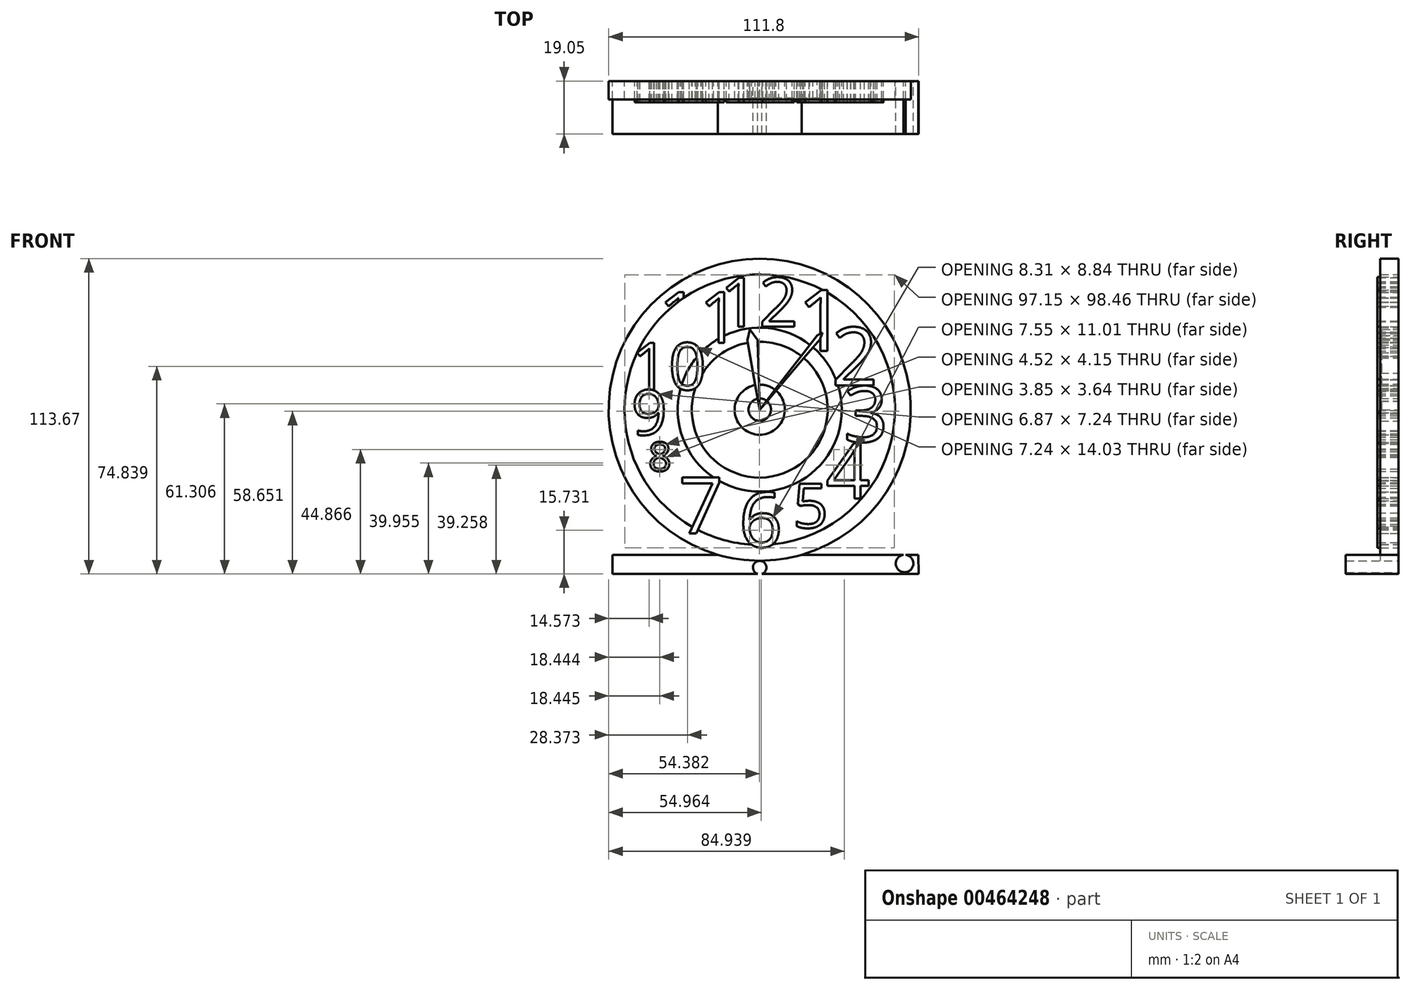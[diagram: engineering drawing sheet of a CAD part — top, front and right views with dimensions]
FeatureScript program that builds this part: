
annotation { "Feature Type Name" : "Feature", "Feature Type Description" : "" }
export const myFeature = defineFeature(function(context is Context, id is Id, definition is map)
    precondition{}
    {
        {
            var Q0;
            Q0=qCreatedBy(makeId("Front.planeOp"),FACE);
            var sketch = newSketch(context, id + "F0", { "sketchPlane" : qUnion([Q0])});
            skCircle(sketch, "E0", {"center": v(0, 0) * mm, "radius": 54.46 * mm});
            skCircle(sketch, "E1", {"center": v(0, 0) * mm, "radius": 48.75 * mm});
            skCircle(sketch, "E2", {"center": v(0, 0) * mm, "radius": 29.56 * mm});
            skCircle(sketch, "E3", {"center": v(0, 0) * mm, "radius": 24.49 * mm});
            skText(sketch, "E4", { "text": "12\n", "fontName": "OpenSans-Regular.ttf"});
            skText(sketch, "E5", { "text": "1", "fontName": "OpenSans-Regular.ttf"});
            skText(sketch, "E6", { "text": "2", "fontName": "OpenSans-Regular.ttf"});
            skText(sketch, "E7", { "text": "3", "fontName": "OpenSans-Regular.ttf"});
            skText(sketch, "E8", { "text": "6", "fontName": "OpenSans-Regular.ttf"});
            skText(sketch, "E9", { "text": "5", "fontName": "OpenSans-Regular.ttf"});
            skText(sketch, "E10", { "text": "4", "fontName": "OpenSans-Regular.ttf"});
            skText(sketch, "E11", { "text": "11", "fontName": "OpenSans-Regular.ttf"});
            skText(sketch, "E12", { "text": "9", "fontName": "OpenSans-Regular.ttf"});
            skText(sketch, "E13", { "text": "10", "fontName": "OpenSans-Regular.ttf"});
            skText(sketch, "E14", { "text": "8", "fontName": "OpenSans-Regular.ttf"});
            skText(sketch, "E15", { "text": "7", "fontName": "OpenSans-Regular.ttf"});
            skCircle(sketch, "E16", {"center": v(0, 0) * mm, "radius": 9.03 * mm});
            skCircle(sketch, "E17", {"center": v(0, 0) * mm, "radius": 4.03 * mm});
            skLineSegment(sketch, "E18", {"start": v(0, 0) * mm, "end": v(-4.5, 25.14) * mm});
            skLineSegment(sketch, "E19", {"start": v(-4.5, 25.14) * mm, "end": v(-3.56, 28.91) * mm});
            skLineSegment(sketch, "E20", {"start": v(-3.56, 28.91) * mm, "end": v(-0.78, 25.14) * mm});
            skLineSegment(sketch, "E21", {"start": v(-0.78, 25.14) * mm, "end": v(0, 0) * mm});
            skLineSegment(sketch, "E22", {"start": v(0, 0) * mm, "end": v(20.68, 26.76) * mm});
            skLineSegment(sketch, "E23", {"start": v(20.68, 26.76) * mm, "end": v(22.61, 27.76) * mm});
            skLineSegment(sketch, "E24", {"start": v(22.61, 27.76) * mm, "end": v(21.81, 25.52) * mm});
            skLineSegment(sketch, "E25", {"start": v(21.81, 25.52) * mm, "end": v(0, 0) * mm});
            skLineSegment(sketch, "E26", {"start": v(-53.12, -52.33) * mm, "end": v(57.12, -52.33) * mm});
            skLineSegment(sketch, "E27", {"start": v(57.12, -52.33) * mm, "end": v(57.34, -59.21) * mm});
            skLineSegment(sketch, "E28", {"start": v(57.34, -59.21) * mm, "end": v(-53.12, -59.21) * mm});
            skLineSegment(sketch, "E29", {"start": v(-53.12, -59.21) * mm, "end": v(-53.12, -52.33) * mm});
            skPoint(sketch, "E30.centerSnap0", {"position": v(57.23, -55.77) * mm});
            skCircle(sketch, "E31", {"center": v(-49.3, -55.6) * mm, "radius": 3.18 * mm});
            skCircle(sketch, "E32", {"center": v(0, -56.93) * mm, "radius": 2.43 * mm});
            skCircle(sketch, "E33", {"center": v(52.2, -55.47) * mm, "radius": 3.18 * mm});
            skCircle(sketch, "E34", {"center": v(29.12, -55.7) * mm, "radius": 2.92 * mm});
            skCircle(sketch, "E35", {"center": v(-30.34, -55.97) * mm, "radius": 3.18 * mm});
            const initialGuessF0  = {"E4": [-0.01435, 0.03, 1, 0, 0.0177], "E5": [0.0136, 0.0212, 1, 0, 0.02213], "E6": [0.02586, 0.00874, 1, 0, 0.02106], "E7": [0.03022, -0.0116, 1, 0, 0.02018], "E8": [-0.0075, -0.04952, 1, 0, 0.01977], "E9": [0.01192, -0.04259, 1, 0, 0.01608], "E10": [0.02386, -0.03208, 1, 0, 0.02006], "E11": [-0.03635, 0.02415, 1, 0, 0.01842], "E12": [-0.0463, -0.00907, 1, 0, 0.01626], "E13": [-0.0463, 0.0072, 1, 0, 0.01698], "E14": [-0.04019, -0.02215, 1, 0, 0.01053], "E15": [-0.02926, -0.04459, 1, 0, 0.02029]};
            skSetInitialGuess(sketch, initialGuessF0);
            skSolve(sketch);
        }
        {
            var Q0;
            {var subQ0=sQuery(id+"F0.wireOp",EDGE,"E26");var subQ1=sQuery(id+"F0.wireOp",EDGE,"E0");var subQ2=makeQuery(id+"F0.imprint","INTERSECT",VERTEX,{"disambiguationData":[OD(0.0)],"derivedFrom":[subQ1,subQ0]});Q0=makeQuery(id+"F0.imprint","IMPRINT",FACE,{"disambiguationData":[TD([[makeQuery(id+"F0.imprint","IMPRINT",EDGE,{"disambiguationData":[TD([[subQ2,-1.0]])],"derivedFrom":subQ1}),1.0]])]});}
            var Q1;
            {var subQ0=sQuery(id+"F0.wireOp",EDGE,"E11.sketch_text.stroke-3");Q1=makeQuery(id+"F0.imprint","IMPRINT",FACE,{"disambiguationData":[TD([[makeQuery(id+"F0.imprint","IMPRINT",EDGE,{"derivedFrom":subQ0}),1.0]])]});}
            var Q2;
            {var subQ1=sQuery(id+"F0.wireOp",EDGE,"E11.sketch_text.stroke-9");Q2=makeQuery(id+"F0.imprint","IMPRINT",FACE,{"disambiguationData":[TD([[makeQuery(id+"F0.imprint","IMPRINT",EDGE,{"derivedFrom":subQ1}),1.0]])]});}
            var Q3;
            {var subQ6=sQuery(id+"F0.wireOp",EDGE,"E6.sketch_text.stroke-1");Q3=makeQuery(id+"F0.imprint","IMPRINT",FACE,{"disambiguationData":[TD([[makeQuery(id+"F0.imprint","IMPRINT",EDGE,{"derivedFrom":subQ6}),1.0]])]});}
            var Q4;
            {var subQ0=sQuery(id+"F0.wireOp",EDGE,"E13.sketch_text.stroke-19");Q4=makeQuery(id+"F0.imprint","IMPRINT",FACE,{"disambiguationData":[TD([[makeQuery(id+"F0.imprint","IMPRINT",EDGE,{"derivedFrom":subQ0}),1.0]])]});}
            var Q5;
            {var subQ0=sQuery(id+"F0.wireOp",EDGE,"E25");var subQ1=sQuery(id+"F0.wireOp",EDGE,"E16");var subQ2=makeQuery(id+"F0.imprint","INTERSECT",VERTEX,{"derivedFrom":[subQ1,subQ0]});Q5=makeQuery(id+"F0.imprint","IMPRINT",FACE,{"disambiguationData":[TD([[makeQuery(id+"F0.imprint","IMPRINT",EDGE,{"disambiguationData":[TD([[subQ2,1.0]])],"derivedFrom":subQ1}),1.0]])]});}
            var Q6;
            {var subQ0=sQuery(id+"F0.wireOp",EDGE,"E22");var subQ1=sQuery(id+"F0.wireOp",EDGE,"E16");var subQ2=makeQuery(id+"F0.imprint","INTERSECT",VERTEX,{"derivedFrom":[subQ1,subQ0]});Q6=makeQuery(id+"F0.imprint","IMPRINT",FACE,{"disambiguationData":[TD([[makeQuery(id+"F0.imprint","IMPRINT",EDGE,{"disambiguationData":[TD([[subQ2,-1.0]])],"derivedFrom":subQ1}),1.0]])]});}
            extrude(context, id + "F1", {"entities" : qUnion([Q0, Q1, Q2, Q3, Q4, Q5, Q6]), "depth" : 6.6 * mm});
        }
        {
            var Q0;
            {var subQ0=sQuery(id+"F0.wireOp",EDGE,"E25");var subQ1=sQuery(id+"F0.wireOp",EDGE,"E2");var subQ2=makeQuery(id+"F0.imprint","INTERSECT",VERTEX,{"derivedFrom":[subQ1,subQ0]});Q0=makeQuery(id+"F0.imprint","IMPRINT",FACE,{"disambiguationData":[TD([[makeQuery(id+"F0.imprint","IMPRINT",EDGE,{"disambiguationData":[TD([[subQ2,-1.0]])],"derivedFrom":subQ1}),1.0]])]});}
            var Q1;
            {var subQ0=sQuery(id+"F0.wireOp",EDGE,"E22");var subQ1=sQuery(id+"F0.wireOp",EDGE,"E3");var subQ2=makeQuery(id+"F0.imprint","INTERSECT",VERTEX,{"derivedFrom":[subQ1,subQ0]});Q1=makeQuery(id+"F0.imprint","IMPRINT",FACE,{"disambiguationData":[TD([[makeQuery(id+"F0.imprint","IMPRINT",EDGE,{"disambiguationData":[TD([[subQ2,1.0]])],"derivedFrom":subQ1}),1.0]])]});}
            var Q2;
            {var subQ0=sQuery(id+"F0.wireOp",EDGE,"E22");var subQ1=sQuery(id+"F0.wireOp",EDGE,"E16");var subQ2=makeQuery(id+"F0.imprint","INTERSECT",VERTEX,{"derivedFrom":[subQ1,subQ0]});Q2=makeQuery(id+"F0.imprint","IMPRINT",FACE,{"disambiguationData":[TD([[makeQuery(id+"F0.imprint","IMPRINT",EDGE,{"disambiguationData":[TD([[subQ2,1.0]])],"derivedFrom":subQ1}),1.0]])]});}
            var Q3;
            {var subQ0=sQuery(id+"F0.wireOp",EDGE,"E21");var subQ1=sQuery(id+"F0.wireOp",EDGE,"E16");var subQ2=makeQuery(id+"F0.imprint","INTERSECT",VERTEX,{"derivedFrom":[subQ1,subQ0]});Q3=makeQuery(id+"F0.imprint","IMPRINT",FACE,{"disambiguationData":[TD([[makeQuery(id+"F0.imprint","IMPRINT",EDGE,{"disambiguationData":[TD([[subQ2,-1.0]])],"derivedFrom":subQ1}),1.0]])]});}
            var Q4;
            {var subQ0=sQuery(id+"F0.wireOp",EDGE,"E21");var subQ1=sQuery(id+"F0.wireOp",EDGE,"E17");var subQ2=makeQuery(id+"F0.imprint","INTERSECT",VERTEX,{"derivedFrom":[subQ1,subQ0]});Q4=makeQuery(id+"F0.imprint","IMPRINT",FACE,{"disambiguationData":[TD([[makeQuery(id+"F0.imprint","IMPRINT",EDGE,{"disambiguationData":[TD([[subQ2,-1.0]])],"derivedFrom":subQ1}),1.0]])]});}
            var Q5;
            {var subQ0=sQuery(id+"F0.wireOp",EDGE,"E22");var subQ1=sQuery(id+"F0.wireOp",EDGE,"E17");var subQ2=makeQuery(id+"F0.imprint","INTERSECT",VERTEX,{"derivedFrom":[subQ1,subQ0]});Q5=makeQuery(id+"F0.imprint","IMPRINT",FACE,{"disambiguationData":[TD([[makeQuery(id+"F0.imprint","IMPRINT",EDGE,{"disambiguationData":[TD([[subQ2,1.0]])],"derivedFrom":subQ1}),1.0]])]});}
            var Q6;
            {var subQ1=sQuery(id+"F0.wireOp",EDGE,"E19");Q6=makeQuery(id+"F0.imprint","IMPRINT",FACE,{"disambiguationData":[TD([[makeQuery(id+"F0.imprint","IMPRINT",EDGE,{"derivedFrom":subQ1}),-1.0]])]});}
            var Q7;
            {var subQ0=sQuery(id+"F0.wireOp",EDGE,"E21");var subQ1=sQuery(id+"F0.wireOp",EDGE,"E3");var subQ2=makeQuery(id+"F0.imprint","INTERSECT",VERTEX,{"derivedFrom":[subQ1,subQ0]});Q7=makeQuery(id+"F0.imprint","IMPRINT",FACE,{"disambiguationData":[TD([[makeQuery(id+"F0.imprint","IMPRINT",EDGE,{"disambiguationData":[TD([[subQ2,-1.0]])],"derivedFrom":subQ1}),1.0]])]});}
            var Q8;
            {var subQ7=sQuery(id+"F0.wireOp",EDGE,"E2");var subQ9=sQuery(id+"F0.wireOp",EDGE,"E25");var subQ10=makeQuery(id+"F0.imprint","INTERSECT",VERTEX,{"derivedFrom":[subQ7,subQ9]});Q8=makeQuery(id+"F0.imprint","IMPRINT",FACE,{"disambiguationData":[TD([[makeQuery(id+"F0.imprint","IMPRINT",EDGE,{"disambiguationData":[TD([[subQ10,-1.0]])],"derivedFrom":subQ7}),-1.0]])]});}
            var Q9;
            {var subQ0=sQuery(id+"F0.wireOp",EDGE,"E24");var subQ1=sQuery(id+"F0.wireOp",EDGE,"E5.sketch_text.stroke-1");var subQ2=makeQuery(id+"F0.imprint","INTERSECT",VERTEX,{"derivedFrom":[subQ1,subQ0]});Q9=makeQuery(id+"F0.imprint","IMPRINT",FACE,{"disambiguationData":[TD([[makeQuery(id+"F0.imprint","IMPRINT",EDGE,{"disambiguationData":[TD([[subQ2,-1.0]])],"derivedFrom":subQ1}),-1.0]])]});}
            extrude(context, id + "F2", {"entities" : qUnion([Q0, Q1, Q2, Q3, Q4, Q5, Q6, Q7, Q8, Q9]), "depth" : 6.1 * mm});
        }
        {
            var Q0;
            Q0=makeQuery(id+"F0.imprint","IMPRINT",FACE,{"disambiguationData":[TD([[makeQuery(id+"F0.imprint","IMPRINT",EDGE,{"derivedFrom":sQuery(id+"F0.wireOp",EDGE,"E4.sketch_text.stroke-0")}),-1.0]])]});
            var Q1;
            Q1=makeQuery(id+"F0.imprint","IMPRINT",FACE,{"disambiguationData":[TD([[makeQuery(id+"F0.imprint","IMPRINT",EDGE,{"derivedFrom":sQuery(id+"F0.wireOp",EDGE,"E4.sketch_text.stroke-9")}),-1.0]])]});
            var Q2;
            {var subQ7=sQuery(id+"F0.wireOp",EDGE,"E5.sketch_text.stroke-0");Q2=makeQuery(id+"F0.imprint","IMPRINT",FACE,{"disambiguationData":[TD([[makeQuery(id+"F0.imprint","IMPRINT",EDGE,{"derivedFrom":subQ7}),-1.0]])]});}
            var Q3;
            {var subQ0=sQuery(id+"F0.wireOp",EDGE,"E5.sketch_text.stroke-7");var subQ1=sQuery(id+"F0.wireOp",EDGE,"E1");var subQ2=makeQuery(id+"F0.imprint","INTERSECT",VERTEX,{"derivedFrom":[subQ1,subQ0]});Q3=makeQuery(id+"F0.imprint","IMPRINT",FACE,{"disambiguationData":[TD([[makeQuery(id+"F0.imprint","IMPRINT",EDGE,{"disambiguationData":[TD([[subQ2,1.0]])],"derivedFrom":subQ1}),-1.0]])]});}
            var Q4;
            {var subQ6=sQuery(id+"F0.wireOp",EDGE,"E6.sketch_text.stroke-3");Q4=makeQuery(id+"F0.imprint","IMPRINT",FACE,{"disambiguationData":[TD([[makeQuery(id+"F0.imprint","IMPRINT",EDGE,{"derivedFrom":subQ6}),-1.0]])]});}
            var Q5;
            {var subQ5=sQuery(id+"F0.wireOp",EDGE,"E6.sketch_text.stroke-1");Q5=makeQuery(id+"F0.imprint","IMPRINT",FACE,{"disambiguationData":[TD([[makeQuery(id+"F0.imprint","IMPRINT",EDGE,{"derivedFrom":subQ5}),-1.0]])]});}
            var Q6;
            Q6=makeQuery(id+"F0.imprint","IMPRINT",FACE,{"disambiguationData":[TD([[makeQuery(id+"F0.imprint","IMPRINT",EDGE,{"derivedFrom":sQuery(id+"F0.wireOp",EDGE,"E7.sketch_text.stroke-0")}),-1.0]])]});
            var Q7;
            Q7=makeQuery(id+"F0.imprint","IMPRINT",FACE,{"disambiguationData":[TD([[makeQuery(id+"F0.imprint","IMPRINT",EDGE,{"derivedFrom":sQuery(id+"F0.wireOp",EDGE,"E10.sketch_text.stroke-0")}),-1.0]])]});
            var Q8;
            Q8=makeQuery(id+"F0.imprint","IMPRINT",FACE,{"disambiguationData":[TD([[makeQuery(id+"F0.imprint","IMPRINT",EDGE,{"derivedFrom":sQuery(id+"F0.wireOp",EDGE,"E9.sketch_text.stroke-0")}),-1.0]])]});
            var Q9;
            Q9=makeQuery(id+"F0.imprint","IMPRINT",FACE,{"disambiguationData":[TD([[makeQuery(id+"F0.imprint","IMPRINT",EDGE,{"derivedFrom":sQuery(id+"F0.wireOp",EDGE,"E8.sketch_text.stroke-0")}),-1.0]])]});
            var Q10;
            {var subQ0=sQuery(id+"F0.wireOp",EDGE,"E8.sketch_text.stroke-13");var subQ1=sQuery(id+"F0.wireOp",EDGE,"E1");var subQ2=makeQuery(id+"F0.imprint","INTERSECT",VERTEX,{"derivedFrom":[subQ1,subQ0]});Q10=makeQuery(id+"F0.imprint","IMPRINT",FACE,{"disambiguationData":[TD([[makeQuery(id+"F0.imprint","IMPRINT",EDGE,{"disambiguationData":[TD([[subQ2,-1.0]])],"derivedFrom":subQ1}),-1.0]])]});}
            var Q11;
            {var subQ0=sQuery(id+"F0.wireOp",EDGE,"E15.sketch_text.stroke-1");Q11=makeQuery(id+"F0.imprint","IMPRINT",FACE,{"disambiguationData":[TD([[makeQuery(id+"F0.imprint","IMPRINT",EDGE,{"derivedFrom":subQ0}),-1.0]])]});}
            var Q12;
            {var subQ0=sQuery(id+"F0.wireOp",EDGE,"E15.sketch_text.stroke-3");var subQ1=sQuery(id+"F0.wireOp",EDGE,"E2");var subQ2=makeQuery(id+"F0.imprint","INTERSECT",VERTEX,{"derivedFrom":[subQ1,subQ0]});Q12=makeQuery(id+"F0.imprint","IMPRINT",FACE,{"disambiguationData":[TD([[makeQuery(id+"F0.imprint","IMPRINT",EDGE,{"disambiguationData":[TD([[subQ2,-1.0]])],"derivedFrom":subQ1}),1.0]])]});}
            var Q13;
            {var subQ5=sQuery(id+"F0.wireOp",EDGE,"E15.sketch_text.stroke-6");Q13=makeQuery(id+"F0.imprint","IMPRINT",FACE,{"disambiguationData":[TD([[makeQuery(id+"F0.imprint","IMPRINT",EDGE,{"derivedFrom":subQ5}),-1.0]])]});}
            var Q14;
            Q14=makeQuery(id+"F0.imprint","IMPRINT",FACE,{"disambiguationData":[TD([[makeQuery(id+"F0.imprint","IMPRINT",EDGE,{"derivedFrom":sQuery(id+"F0.wireOp",EDGE,"E14.sketch_text.stroke-0")}),-1.0]])]});
            var Q15;
            Q15=makeQuery(id+"F0.imprint","IMPRINT",FACE,{"disambiguationData":[TD([[makeQuery(id+"F0.imprint","IMPRINT",EDGE,{"derivedFrom":sQuery(id+"F0.wireOp",EDGE,"E12.sketch_text.stroke-0")}),-1.0]])]});
            var Q16;
            {var subQ0=sQuery(id+"F0.wireOp",EDGE,"E13.sketch_text.stroke-2");Q16=makeQuery(id+"F0.imprint","IMPRINT",FACE,{"disambiguationData":[TD([[makeQuery(id+"F0.imprint","IMPRINT",EDGE,{"derivedFrom":subQ0}),-1.0]])]});}
            var Q17;
            {var subQ14=sQuery(id+"F0.wireOp",EDGE,"E13.sketch_text.stroke-12");Q17=makeQuery(id+"F0.imprint","IMPRINT",FACE,{"disambiguationData":[TD([[makeQuery(id+"F0.imprint","IMPRINT",EDGE,{"derivedFrom":subQ14}),-1.0]])]});}
            var Q18;
            {var subQ1=sQuery(id+"F0.wireOp",EDGE,"E13.sketch_text.stroke-19");Q18=makeQuery(id+"F0.imprint","IMPRINT",FACE,{"disambiguationData":[TD([[makeQuery(id+"F0.imprint","IMPRINT",EDGE,{"derivedFrom":subQ1}),-1.0]])]});}
            var Q19;
            {var subQ0=sQuery(id+"F0.wireOp",EDGE,"E13.sketch_text.stroke-9");var subQ1=sQuery(id+"F0.wireOp",EDGE,"E3");var subQ2=makeQuery(id+"F0.imprint","INTERSECT",VERTEX,{"derivedFrom":[subQ1,subQ0]});Q19=makeQuery(id+"F0.imprint","IMPRINT",FACE,{"disambiguationData":[TD([[makeQuery(id+"F0.imprint","IMPRINT",EDGE,{"disambiguationData":[TD([[subQ2,-1.0]])],"derivedFrom":subQ1}),1.0]])]});}
            var Q20;
            {var subQ0=sQuery(id+"F0.wireOp",EDGE,"E11.sketch_text.stroke-11");Q20=makeQuery(id+"F0.imprint","IMPRINT",FACE,{"disambiguationData":[TD([[makeQuery(id+"F0.imprint","IMPRINT",EDGE,{"derivedFrom":subQ0}),-1.0]])]});}
            var Q21;
            {var subQ5=sQuery(id+"F0.wireOp",EDGE,"E11.sketch_text.stroke-9");Q21=makeQuery(id+"F0.imprint","IMPRINT",FACE,{"disambiguationData":[TD([[makeQuery(id+"F0.imprint","IMPRINT",EDGE,{"derivedFrom":subQ5}),-1.0]])]});}
            var Q22;
            {var subQ4=sQuery(id+"F0.wireOp",EDGE,"E11.sketch_text.stroke-0");Q22=makeQuery(id+"F0.imprint","IMPRINT",FACE,{"disambiguationData":[TD([[makeQuery(id+"F0.imprint","IMPRINT",EDGE,{"derivedFrom":subQ4}),-1.0]])]});}
            var Q23;
            {var subQ0=sQuery(id+"F0.wireOp",EDGE,"E11.sketch_text.stroke-3");Q23=makeQuery(id+"F0.imprint","IMPRINT",FACE,{"disambiguationData":[TD([[makeQuery(id+"F0.imprint","IMPRINT",EDGE,{"derivedFrom":subQ0}),-1.0]])]});}
            extrude(context, id + "F3", {"entities" : qUnion([Q0, Q1, Q2, Q3, Q4, Q5, Q6, Q7, Q8, Q9, Q10, Q11, Q12, Q13, Q14, Q15, Q16, Q17, Q18, Q19, Q20, Q21, Q22, Q23]), "depth" : 7.62 * mm});
        }
        {
            var Q0;
            {var subQ0=sQuery(id+"F0.wireOp",EDGE,"DknU1P71-qqUr-9apj-mGy3-QRReveRhXF4h");var subQ1=sQuery(id+"F0.wireOp",EDGE,"E26");var subQ2=makeQuery(id+"F0.imprint","INTERSECT",VERTEX,{"disambiguationData":[OD(1.0)],"derivedFrom":[subQ1,subQ0]});Q0=makeQuery(id+"F0.imprint","IMPRINT",FACE,{"disambiguationData":[TD([[makeQuery(id+"F0.imprint","IMPRINT",EDGE,{"disambiguationData":[TD([[subQ2,-1.0]])],"derivedFrom":subQ1}),-1.0]])]});}
            var Q1;
            {var subQ3=sQuery(id+"F0.wireOp",EDGE,"E0");var subQ7=sQuery(id+"F0.wireOp",EDGE,"E26");var subQ9=makeQuery(id+"F0.imprint","INTERSECT",VERTEX,{"disambiguationData":[OD(1.0)],"derivedFrom":[subQ3,subQ7]});Q1=makeQuery(id+"F0.imprint","IMPRINT",FACE,{"disambiguationData":[TD([[makeQuery(id+"F0.imprint","IMPRINT",EDGE,{"disambiguationData":[TD([[subQ9,1.0]])],"derivedFrom":subQ3}),-1.0]])]});}
            var Q2;
            {var subQ3=sQuery(id+"F0.wireOp",EDGE,"E0");var subQ5=sQuery(id+"F0.wireOp",EDGE,"E26");var subQ6=makeQuery(id+"F0.imprint","INTERSECT",VERTEX,{"disambiguationData":[OD(0.0)],"derivedFrom":[subQ3,subQ5]});Q2=makeQuery(id+"F0.imprint","IMPRINT",FACE,{"disambiguationData":[TD([[makeQuery(id+"F0.imprint","IMPRINT",EDGE,{"disambiguationData":[TD([[subQ6,-1.0]])],"derivedFrom":subQ3}),-1.0]])]});}
            var Q3;
            {var subQ0=sQuery(id+"F0.wireOp",EDGE,"KBSSTNhy-3uzt-HHLB-lN4G-C7P4vr1EewhW");var subQ1=sQuery(id+"F0.wireOp",EDGE,"E26");var subQ2=makeQuery(id+"F0.imprint","INTERSECT",VERTEX,{"derivedFrom":[subQ1,subQ0]});Q3=makeQuery(id+"F0.imprint","IMPRINT",FACE,{"disambiguationData":[TD([[makeQuery(id+"F0.imprint","IMPRINT",EDGE,{"disambiguationData":[TD([[subQ2,-1.0]])],"derivedFrom":subQ1}),-1.0]])]});}
            var Q4;
            {var subQ0=sQuery(id+"F0.wireOp",EDGE,"E28");var subQ1=sQuery(id+"F0.wireOp",EDGE,"E27");var subQ2=makeQuery(id+"F0.imprint","INTERSECT",VERTEX,{"derivedFrom":[subQ1,subQ0]});Q4=makeQuery(id+"F0.imprint","IMPRINT",FACE,{"disambiguationData":[TD([[makeQuery(id+"F0.imprint","IMPRINT",EDGE,{"disambiguationData":[TD([[subQ2,1.0]])],"derivedFrom":subQ1}),-1.0]])]});}
            var Q5;
            {var subQ0=sQuery(id+"F0.wireOp",EDGE,"E27");var subQ1=sQuery(id+"F0.wireOp",EDGE,"E26");var subQ2=makeQuery(id+"F0.imprint","INTERSECT",VERTEX,{"derivedFrom":[subQ1,subQ0]});Q5=makeQuery(id+"F0.imprint","IMPRINT",FACE,{"disambiguationData":[TD([[makeQuery(id+"F0.imprint","IMPRINT",EDGE,{"disambiguationData":[TD([[subQ2,1.0]])],"derivedFrom":subQ1}),-1.0]])]});}
            extrude(context, id + "F4", {"entities" : qUnion([Q0, Q1, Q2, Q3, Q4, Q5]), "operationType" : NewBodyOperationType.ADD, "depth" : 7.11 * mm});
        }
        {
            var Q0;
            Q0=makeQuery(id+"F0.imprint","IMPRINT",FACE,{"disambiguationData":[TD([[makeQuery(id+"F0.imprint","IMPRINT",EDGE,{"derivedFrom":sQuery(id+"F0.wireOp",EDGE,"E35")}),1.0]])]});
            var Q1;
            Q1=makeQuery(id+"F0.imprint","IMPRINT",FACE,{"disambiguationData":[TD([[makeQuery(id+"F0.imprint","IMPRINT",EDGE,{"derivedFrom":sQuery(id+"F0.wireOp",EDGE,"E31")}),1.0]])]});
            var Q2;
            {var subQ0=sQuery(id+"F0.wireOp",EDGE,"E32");var subQ1=sQuery(id+"F0.wireOp",EDGE,"E28");var subQ2=makeQuery(id+"F0.imprint","INTERSECT",VERTEX,{"disambiguationData":[OD(0.0)],"derivedFrom":[subQ1,subQ0]});Q2=makeQuery(id+"F0.imprint","IMPRINT",FACE,{"disambiguationData":[TD([[makeQuery(id+"F0.imprint","IMPRINT",EDGE,{"disambiguationData":[TD([[subQ2,-1.0]])],"derivedFrom":subQ1}),-1.0]])]});}
            var Q3;
            Q3=makeQuery(id+"F0.imprint","IMPRINT",FACE,{"disambiguationData":[TD([[makeQuery(id+"F0.imprint","IMPRINT",EDGE,{"derivedFrom":sQuery(id+"F0.wireOp",EDGE,"E34")}),1.0]])]});
            var Q4;
            {var subQ0=sQuery(id+"F0.wireOp",EDGE,"E33");var subQ1=sQuery(id+"F0.wireOp",EDGE,"E26");var subQ2=makeQuery(id+"F0.imprint","INTERSECT",VERTEX,{"disambiguationData":[OD(0.0)],"derivedFrom":[subQ1,subQ0]});Q4=makeQuery(id+"F0.imprint","IMPRINT",FACE,{"disambiguationData":[TD([[makeQuery(id+"F0.imprint","IMPRINT",EDGE,{"disambiguationData":[TD([[subQ2,-1.0]])],"derivedFrom":subQ1}),-1.0]])]});}
            extrude(context, id + "F5", {"entities" : qUnion([Q0, Q1, Q2, Q3, Q4]), "operationType" : NewBodyOperationType.ADD, "depth" : 19.05 * mm});
        }
    });
